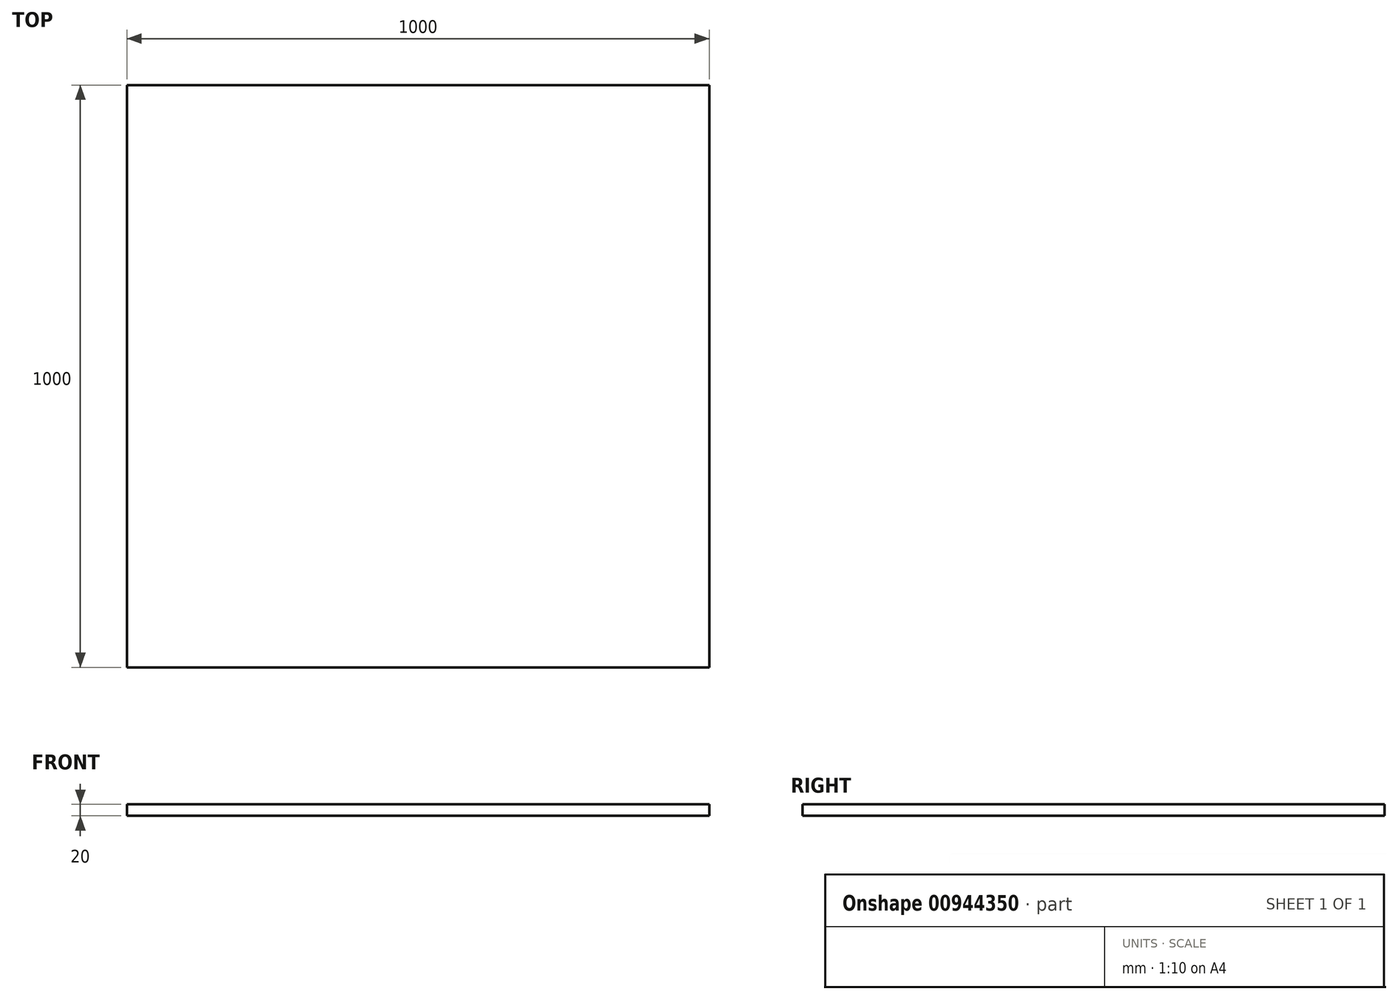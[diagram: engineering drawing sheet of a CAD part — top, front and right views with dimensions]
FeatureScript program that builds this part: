
annotation { "Feature Type Name" : "Feature", "Feature Type Description" : "" }
export const myFeature = defineFeature(function(context is Context, id is Id, definition is map)
    precondition{}
    {
        {
            var Q0;
            Q0=qCreatedBy(makeId("Top.planeOp"),FACE);
            var sketch = newSketch(context, id + "F0", { "sketchPlane" : qUnion([Q0])});
            skLineSegment(sketch, "E0", {"start": v(0, 0) * mm, "end": v(0, 1000) * mm});
            skLineSegment(sketch, "E1", {"start": v(0, 1000) * mm, "end": v(1000, 1000) * mm});
            skLineSegment(sketch, "E2", {"start": v(1000, 1000) * mm, "end": v(1000, 0) * mm});
            skLineSegment(sketch, "E3", {"start": v(1000, 0) * mm, "end": v(0, 0) * mm});
            skSolve(sketch);
        }
        {
            var Q0;
            Q0=qCreatedBy(makeId("Front.planeOp"),FACE);
            var sketch = newSketch(context, id + "F1", { "sketchPlane" : qUnion([Q0])});
            skLineSegment(sketch, "E4", {"start": v(0, 0) * mm, "end": v(0, 20) * mm});
            skSolve(sketch);
        }
        {
            var Q0;
            Q0=makeQuery(id+"F0.imprint","IMPRINT",FACE,{"disambiguationData":[TD([[makeQuery(id+"F0.imprint","IMPRINT",EDGE,{"derivedFrom":sQuery(id+"F0.wireOp",EDGE,"E0")}),-1.0]])]});
            var Q1;
            Q1=sQuery(id+"F1.wireOp",EDGE,"E4");
            sweep(context, id + "F2", {"profiles" : qUnion([Q0]), "path" : qUnion([Q1])});
        }
    });
